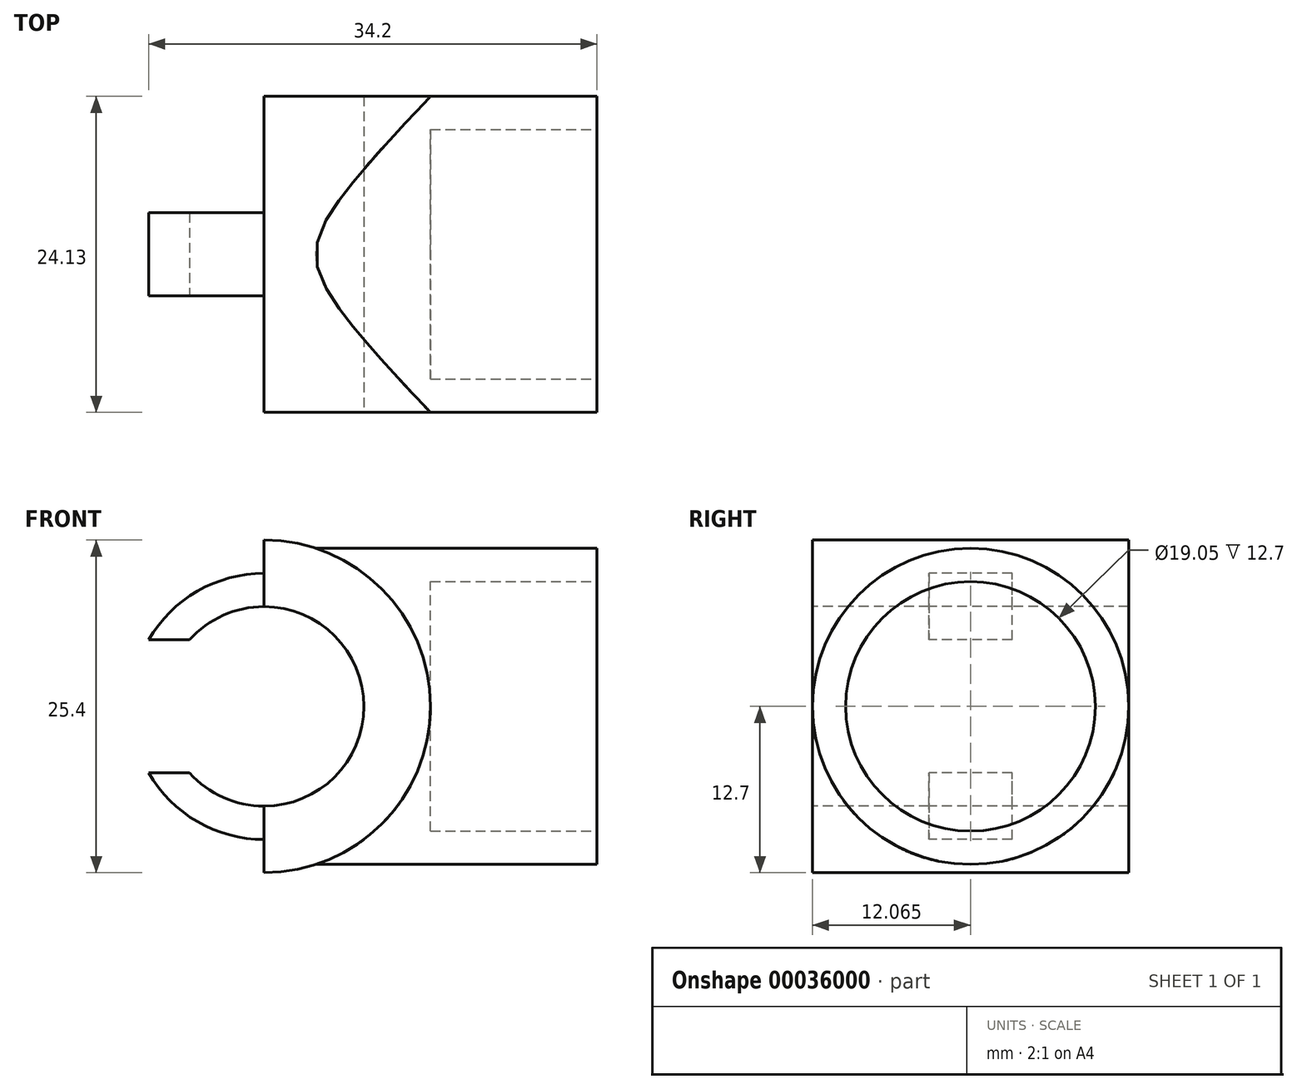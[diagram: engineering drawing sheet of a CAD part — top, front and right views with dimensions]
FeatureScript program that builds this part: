
annotation { "Feature Type Name" : "Feature", "Feature Type Description" : "" }
export const myFeature = defineFeature(function(context is Context, id is Id, definition is map)
    precondition{}
    {
        {
            var Q0;
            Q0=qCreatedBy(makeId("Front.planeOp"),FACE);
            var sketch = newSketch(context, id + "F0", { "sketchPlane" : qUnion([Q0])});
            skCircle(sketch, "E0", {"center": v(0, 0) * mm, "radius": 12.7 * mm});
            skSolve(sketch);
        }
        {
            var Q0;
            Q0=qCreatedBy(makeId("Right.planeOp"),FACE);
            var sketch = newSketch(context, id + "F1", { "sketchPlane" : qUnion([Q0])});
            skCircle(sketch, "E1", {"center": v(-12.07, 0) * mm, "radius": 12.07 * mm});
            skSolve(sketch);
        }
        {
            var Q0;
            Q0=makeQuery(id+"F0.imprint","IMPRINT",FACE,{"disambiguationData":[TD([[makeQuery(id+"F0.imprint","IMPRINT",EDGE,{"derivedFrom":sQuery(id+"F0.wireOp",EDGE,"E0")}),1.0]])]});
            extrude(context, id + "F2", {"entities" : qUnion([Q0]), "depth" : 24.13 * mm});
        }
        {
            var Q0;
            Q0 = qSketchRegion(id + "F1", true);
            extrude(context, id + "F3", {"entities" : qUnion([Q0]), "operationType" : NewBodyOperationType.ADD, "depth" : 25.4 * mm});
        }
        {
            var Q0;
            Q0=makeQuery(id+"F2.opExtrude","CAP_FACE",FACE,{"disambiguationData":[OSD([sQuery(id+"F0.wireOp",EDGE,"E0")])],"isStart":false});
            var sketch = newSketch(context, id + "F4", { "sketchPlane" : qUnion([Q0])});
            skCircle(sketch, "E2", {"center": v(0, 0) * mm, "radius": 7.62 * mm});
            skSolve(sketch);
        }
        {
            var Q0;
            Q0=makeQuery(id+"F4.imprint","IMPRINT",FACE,{"disambiguationData":[TD([[makeQuery(id+"F4.imprint","IMPRINT",EDGE,{"derivedFrom":sQuery(id+"F4.wireOp",EDGE,"E2")}),1.0]])]});
            extrude(context, id + "F5", {"entities" : qUnion([Q0]), "operationType" : NewBodyOperationType.REMOVE, "oppositeDirection" : true, "depth" : 25.4 * mm});
        }
        {
            var Q0;
            Q0=makeQuery(id+"F3.opExtrude","CAP_FACE",FACE,{"disambiguationData":[OSD([sQuery(id+"F1.wireOp",EDGE,"E1")])],"isStart":false});
            var sketch = newSketch(context, id + "F6", { "sketchPlane" : qUnion([Q0])});
            skCircle(sketch, "E3", {"center": v(-12.07, 0) * mm, "radius": 9.53 * mm});
            skSolve(sketch);
        }
        {
            var Q0;
            Q0=makeQuery(id+"F6.imprint","IMPRINT",FACE,{"disambiguationData":[TD([[makeQuery(id+"F6.imprint","IMPRINT",EDGE,{"derivedFrom":sQuery(id+"F6.wireOp",EDGE,"E3")}),1.0]])]});
            var Q1;
            Q1=sQuery(id+"F6.wireOp",EDGE,"E3");
            extrude(context, id + "F7", {"entities" : qUnion([Q0]), "operationType" : NewBodyOperationType.REMOVE, "surfaceEntities" : qUnion([Q1]), "oppositeDirection" : true, "depth" : 12.7 * mm});
        }
        {
            var Q0;
            Q0=qCreatedBy(makeId("Right.planeOp"),FACE);
            var sketch = newSketch(context, id + "F8", { "sketchPlane" : qUnion([Q0])});
            skLineSegment(sketch, "E4.bottom", {"start": v(0, 12.6) * mm, "end": v(-24.13, 12.6) * mm});
            skLineSegment(sketch, "E4.top", {"start": v(0, -12.8) * mm, "end": v(-24.13, -12.8) * mm});
            skLineSegment(sketch, "E4.left", {"start": v(0, 12.6) * mm, "end": v(0, -12.8) * mm});
            skLineSegment(sketch, "E4.right", {"start": v(-24.13, 12.6) * mm, "end": v(-24.13, -12.8) * mm});
            skLineSegment(sketch, "E5.rect.bottom", {"start": v(-15.24, -17.32) * mm, "end": v(-8.9, -17.32) * mm});
            skLineSegment(sketch, "E5.rect.top", {"start": v(-15.24, 17.32) * mm, "end": v(-8.89, 17.32) * mm});
            skLineSegment(sketch, "E5.rect.left", {"start": v(-15.24, -17.32) * mm, "end": v(-15.24, 17.32) * mm});
            skLineSegment(sketch, "E5.rect.right", {"start": v(-8.9, -17.32) * mm, "end": v(-8.89, 17.32) * mm});
            skPoint(sketch, "E5.rect.middle", {"position": v(-12.07, 0) * mm});
            skPoint(sketch, "E5.rect.middle.positionSnap0", {"position": v(-12.07, 12.6) * mm});
            skPoint(sketch, "E5.rect.centerSnap0", {"position": v(-12.07, 12.6) * mm});
            skSolve(sketch);
        }
        {
            var Q0;
            {var subQ5=sQuery(id+"F8.wireOp",EDGE,"E4.right");Q0=makeQuery(id+"F8.imprint","IMPRINT",FACE,{"disambiguationData":[TD([[makeQuery(id+"F8.imprint","IMPRINT",EDGE,{"derivedFrom":subQ5}),1.0]])]});}
            var Q1;
            {var subQ5=sQuery(id+"F8.wireOp",EDGE,"E4.left");Q1=makeQuery(id+"F8.imprint","IMPRINT",FACE,{"disambiguationData":[TD([[makeQuery(id+"F8.imprint","IMPRINT",EDGE,{"derivedFrom":subQ5}),-1.0]])]});}
            extrude(context, id + "F9", {"entities" : qUnion([Q0, Q1]), "operationType" : NewBodyOperationType.REMOVE, "oppositeDirection" : true, "depth" : 25.4 * mm});
        }
        {
            var Q0;
            {var subQ0=sQuery(id+"F8.wireOp",EDGE,"E4.left");var subQ1=sQuery(id+"F8.wireOp",EDGE,"E4.bottom");var subQ2=sQuery(id+"F8.wireOp",EDGE,"E5.rect.right");Q0=makeQuery(id+"F9.boolean.opBoolean","COPY",FACE,{"disambiguationData":[TD([makeQuery(id+"F9.opExtrude","SWEPT_FACE",FACE,{"disambiguationData":[OSD([subQ1]),TDD([makeQuery(id+"F8.imprint","IMPRINT",EDGE,{"disambiguationData":[TD([[makeQuery(id+"F8.imprint","INTERSECT",VERTEX,{"derivedFrom":[subQ1,subQ0]}),-1.0]])],"derivedFrom":subQ1})])]})])],"derivedFrom":makeQuery(id+"F9.opExtrude","CAP_FACE",FACE,{"disambiguationData":[OSD([subQ1,sQuery(id+"F8.wireOp",EDGE,"E4.top"),subQ0,subQ2])],"isStart":true})});}
            var sketch = newSketch(context, id + "F10", { "sketchPlane" : qUnion([Q0])});
            skLineSegment(sketch, "E6.left", {"start": v(8.89, 7.62) * mm, "end": v(8.89, -0.06) * mm});
            skLineSegment(sketch, "E7.top", {"start": v(8.89, 5.08) * mm, "end": v(12.37, 5.08) * mm});
            skLineSegment(sketch, "E8.bottom", {"start": v(8.89, 5.08) * mm, "end": v(15.24, 5.08) * mm});
            skLineSegment(sketch, "E8.top", {"start": v(8.89, -5.08) * mm, "end": v(15.24, -5.08) * mm});
            skLineSegment(sketch, "E8.left", {"start": v(8.89, 5.08) * mm, "end": v(8.89, -5.08) * mm});
            skLineSegment(sketch, "E8.right", {"start": v(15.24, 5.08) * mm, "end": v(15.24, -5.08) * mm});
            skSolve(sketch);
        }
        {
            var Q0;
            {var subQ2=sQuery(id+"F10.wireOp",EDGE,"E8.top");Q0=makeQuery(id+"F10.imprint","IMPRINT",FACE,{"disambiguationData":[TD([[makeQuery(id+"F10.imprint","IMPRINT",EDGE,{"derivedFrom":subQ2}),1.0]])]});}
            extrude(context, id + "F11", {"entities" : qUnion([Q0]), "operationType" : NewBodyOperationType.REMOVE, "depth" : 17.1 * mm});
        }
        {
            var Q0;
            {var subQ3=sQuery(id+"F8.wireOp",EDGE,"E5.rect.left");var subQ4=makeQuery(id+"F9.opExtrude","SWEPT_FACE",FACE,{"disambiguationData":[OSD([subQ3])]});Q0=makeQuery(id+"F11.boolean.opBoolean","SPLIT",FACE,{"disambiguationData":[TD([makeQuery(id+"F11.opExtrude","SWEPT_FACE",FACE,{"disambiguationData":[OSD([sQuery(id+"F10.wireOp",EDGE,"E8.top")])]})])],"derivedFrom":makeQuery(id+"F9.boolean.opBoolean","COPY",FACE,{"derivedFrom":subQ4})});}
            var sketch = newSketch(context, id + "F12", { "sketchPlane" : qUnion([Q0])});
            skLineSegment(sketch, "E9", {"start": v(0, 16.09) * mm, "end": v(0, -15.52) * mm});
            skCircle(sketch, "E10", {"center": v(0, 0) * mm, "radius": 10.16 * mm});
            skCircle(sketch, "E11", {"center": v(0, 0) * mm, "radius": 12.7 * mm});
            skSolve(sketch);
        }
        {
            var Q0;
            {var subQ3=sQuery(id+"F12.wireOp",EDGE,"E11");var subQ5=sQuery(id+"F12.wireOp",EDGE,"E9");var subQ6=makeQuery(id+"F12.imprint","INTERSECT",VERTEX,{"disambiguationData":[OD(1.0)],"derivedFrom":[subQ5,subQ3]});Q0=makeQuery(id+"F12.imprint","IMPRINT",FACE,{"disambiguationData":[TD([[makeQuery(id+"F12.imprint","IMPRINT",EDGE,{"disambiguationData":[TD([[subQ6,-1.0]])],"derivedFrom":subQ5}),-1.0]])]});}
            var Q1;
            {var subQ3=sQuery(id+"F12.wireOp",EDGE,"E11");var subQ5=sQuery(id+"F12.wireOp",EDGE,"E9");var subQ6=makeQuery(id+"F12.imprint","INTERSECT",VERTEX,{"disambiguationData":[OD(0.0)],"derivedFrom":[subQ5,subQ3]});Q1=makeQuery(id+"F12.imprint","IMPRINT",FACE,{"disambiguationData":[TD([[makeQuery(id+"F12.imprint","IMPRINT",EDGE,{"disambiguationData":[TD([[subQ6,-1.0]])],"derivedFrom":subQ5}),1.0]])]});}
            extrude(context, id + "F13", {"entities" : qUnion([Q0, Q1]), "operationType" : NewBodyOperationType.REMOVE, "oppositeDirection" : true, "depth" : 25.4 * mm});
        }
        {
            var Q0;
            {var subQ0=sQuery(id+"F8.wireOp",EDGE,"E4.bottom");Q0=makeQuery(id+"F9.boolean.opBoolean","COPY",FACE,{"derivedFrom":makeQuery(id+"F9.opExtrude","SWEPT_FACE",FACE,{"disambiguationData":[OSD([subQ0]),TDD([makeQuery(id+"F8.imprint","IMPRINT",EDGE,{"disambiguationData":[TD([[makeQuery(id+"F8.imprint","INTERSECT",VERTEX,{"derivedFrom":[subQ0,sQuery(id+"F8.wireOp",EDGE,"E4.right")]}),1.0]])],"derivedFrom":subQ0})])]})});}
            var sketch = newSketch(context, id + "F14", { "sketchPlane" : qUnion([Q0])});
            skLineSegment(sketch, "E12.bottom", {"start": v(-1.58, 24.13) * mm, "end": v(0, 24.13) * mm});
            skLineSegment(sketch, "E12.top", {"start": v(-1.58, 15.24) * mm, "end": v(0, 15.24) * mm});
            skLineSegment(sketch, "E12.left", {"start": v(-1.58, 24.13) * mm, "end": v(-1.58, 15.24) * mm});
            skLineSegment(sketch, "E12.right", {"start": v(0, 24.13) * mm, "end": v(0, 15.24) * mm});
            skSolve(sketch);
        }
        {
            var Q0;
            Q0 = qSketchRegion(id + "F14", true);
            extrude(context, id + "F15", {"entities" : qUnion([Q0]), "operationType" : NewBodyOperationType.REMOVE, "oppositeDirection" : true, "depth" : 25.4 * mm});
        }
    });
